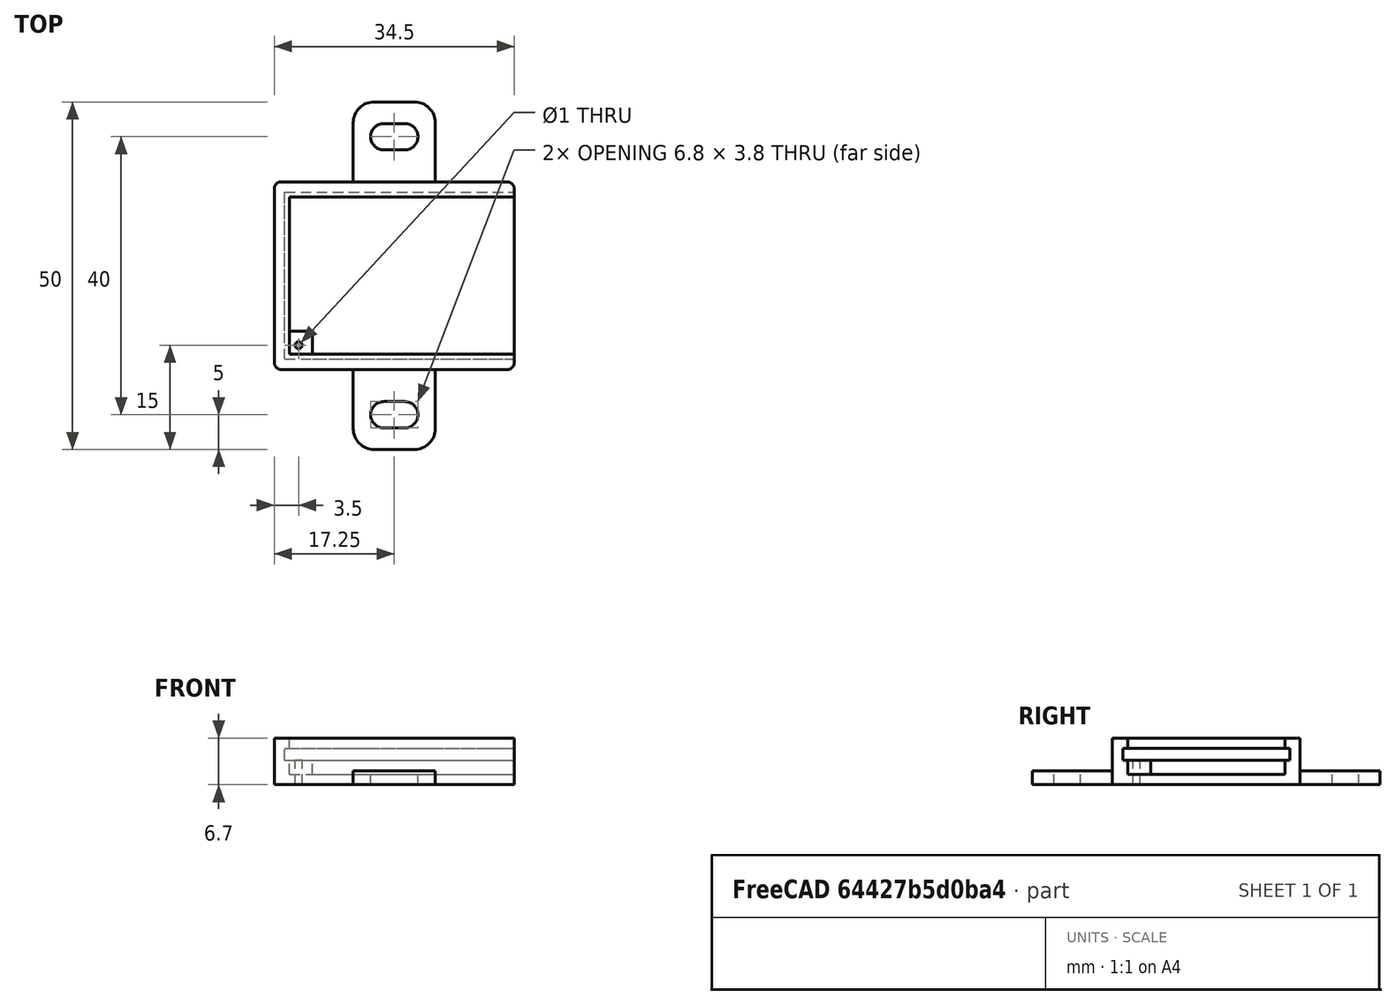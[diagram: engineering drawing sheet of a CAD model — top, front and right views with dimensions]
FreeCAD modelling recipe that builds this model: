
FCSTD DOCUMENT  (FreeCAD 0.19R)
Label: usbB2usbA
License: FreeArt
LicenseURL: http://artlibre.org/licence/lal
objects: Part::Box×4, Part::MultiFuse×3, Part::Cut×2, Spreadsheet::Sheet×1, Part::Fillet×1, Part::Cylinder×1, Part::Feature×1, App::Part×1
note: 12 computed .brp shape members not serialized (recipe doc carries the construction recipe); baked Part::Feature solids carry a one-line shape summary decoded from their .brp

FEATURE [Spreadsheet::Sheet] Spreadsheet  label="p"
  cells = A1=pcb_x; B1(pcb_x)=33; A2=pcb_y; B2(pcb_y)=24; A3=pcb_z; B3(pcb_z)=1.7; A4=pcb_under; B4(pcb_under)=2; A5=side_wall; B5(side_wall)=1.5; A6=pcb_side_lane; B6(pcb_side_lane)=0.7; A7=bottom_wall; B7(bottom_wall)=1.5; A8=pcb_above; B8(pcb_above)=1.5
FEATURE [Part::Box] Box  label="external cube"
  AttacherType = Attacher::AttachEngine3D
  Height = 6.7
  Length = 34.5
  Width = 27
  expr: Height = <<p>>.bottom_wall + <<p>>.pcb_under + <<p>>.pcb_z + <<p>>.pcb_above
  expr: Width = <<p>>.pcb_y + 2 * <<p>>.side_wall
  expr: Length = <<p>>.pcb_x + <<p>>.side_wall
FEATURE [Part::Box] Box006  label="internal cube"
  AttacherType = Attacher::AttachEngine3D
  Height = 5.2
  Length = 33.1
  Placement = pos=(2.2,2.2,1.5) rot=(0,0,1;0rad)
  Width = 22.6
  expr: .Placement.Base.y = <<p>>.side_wall + <<p>>.pcb_side_lane
  expr: .Placement.Base.x = <<p>>.side_wall + <<p>>.pcb_side_lane
  expr: .Placement.Base.z = <<p>>.bottom_wall
  expr: Height = <<p>>.pcb_under + <<p>>.pcb_z + <<p>>.pcb_above
  expr: Width = <<p>>.pcb_y - 2 * <<p>>.pcb_side_lane
  expr: Length = <<p>>.pcb_x - 2 * <<p>>.pcb_side_lane + <<p>>.side_wall
FEATURE [Part::Box] Box007  label="pcb extract cube"
  AttacherType = Attacher::AttachEngine3D
  Height = 1.7
  Length = 33
  Placement = pos=(1.5,1.5,3.5) rot=(0,0,1;0rad)
  Width = 24
  expr: .Placement.Base.y = <<p>>.side_wall
  expr: .Placement.Base.x = <<p>>.side_wall
  expr: Length = <<p>>.pcb_x
  expr: Width = <<p>>.pcb_y
  expr: .Placement.Base.z = <<p>>.bottom_wall + <<p>>.pcb_under
  expr: Height = <<p>>.pcb_z
FEATURE [Part::MultiFuse] Fusion  label="extract fusion"
  Shapes = -> [Box006,Box007]
FEATURE [Part::Fillet] Fillet  label="external fillet"
  Base = -> Box
  Edges = 4 edges r=1: [Edge1,Edge3,Edge5,Edge7]
FEATURE [Part::Box] Box008  label="screw stand"
  AttacherType = Attacher::AttachEngine3D
  Height = 3.5
  Length = 4
  Placement = pos=(1.5,1.5,0) rot=(0,0,1;0rad)
  Width = 4
  expr: .Placement.Base.y = <<p>>.side_wall
  expr: .Placement.Base.x = <<p>>.side_wall
  expr: Height = <<p>>.pcb_under + <<p>>.bottom_wall
FEATURE [Part::Cylinder] Cylinder  label="screw hole"
  Angle = 360
  AttacherType = Attacher::AttachEngine3D
  Height = 10
  Placement = pos=(3.5,3.5,0) rot=(0,0,1;0rad)
  Radius = 0.5
  expr: .Placement.Base.y = <<screw stand>>.Placement.Base.y + <<screw stand>>.Width / 2
  expr: .Placement.Base.x = <<screw stand>>.Placement.Base.x + <<screw stand>>.Length / 2
FEATURE [Part::Feature] Cut002003  label="attach plane y dir002"
  Placement = pos=(11.35,-11.5,0) rot=(0,0,1;0rad)
  shape: bbox 11.8 x 50 x 2 mm, 20 faces (baked)
FEATURE [Part::MultiFuse] Fusion001  label="solid fusion"
  Shapes = -> [Fillet,Cut002003]
FEATURE [Part::Cut] Cut  label="body cut"
  Base = -> Fusion001
  Tool = -> Fusion
FEATURE [Part::MultiFuse] Fusion002  label="body fusion"
  Shapes = -> [Box008,Cut]
FEATURE [Part::Cut] Cut002002  label="body with hole cut"
  Base = -> Fusion002
  Tool = -> Cylinder
FEATURE [App::Part] Part  label="pcb box part"
  Group = -> [Cut002002]
  Origin = -> Origin
